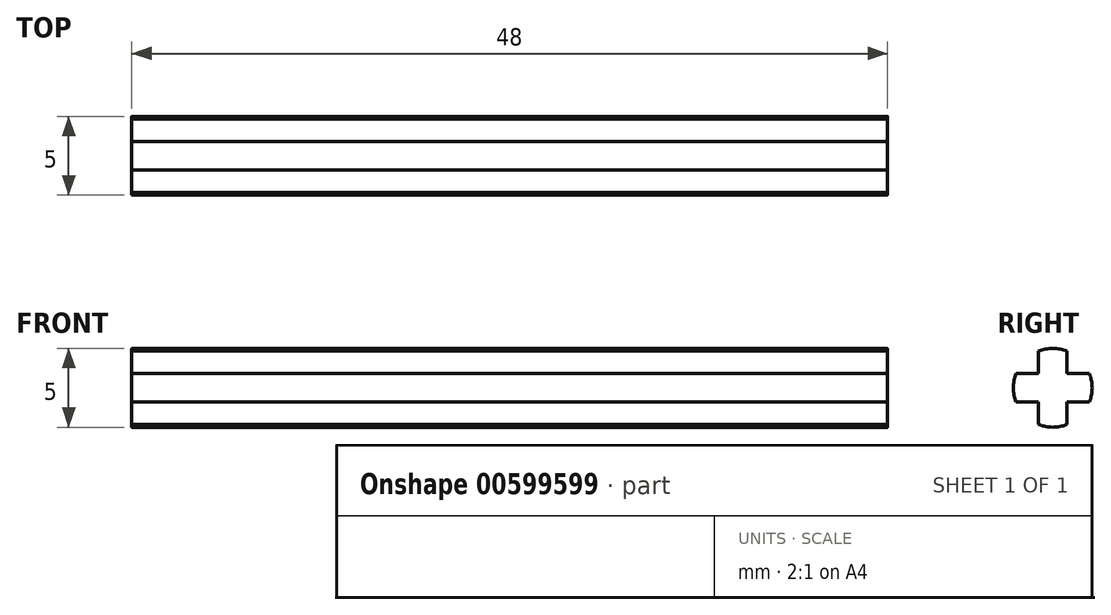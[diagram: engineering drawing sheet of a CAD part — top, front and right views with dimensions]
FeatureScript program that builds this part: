
annotation { "Feature Type Name" : "Feature", "Feature Type Description" : "" }
export const myFeature = defineFeature(function(context is Context, id is Id, definition is map)
    precondition{}
    {
        {
            var Q0;
            Q0=qCreatedBy(makeId("Right.planeOp"),FACE);
            var sketch = newSketch(context, id + "F0", { "sketchPlane" : qUnion([Q0])});
            skArc(sketch, "E0", {"start": v(2.33, -0.9) * mm, "mid": v(2.5, 0) * mm, "end": v(2.33, 0.9) * mm});
            skLineSegment(sketch, "E1.left", {"start": v(-0.9, 2.33) * mm, "end": v(-0.9, 0.9) * mm});
            skLineSegment(sketch, "E1.right", {"start": v(0.9, 2.33) * mm, "end": v(0.9, 0.9) * mm});
            skLineSegment(sketch, "E2.bottom", {"start": v(2.33, 0.9) * mm, "end": v(0.9, 0.9) * mm});
            skLineSegment(sketch, "E2.top", {"start": v(2.33, -0.9) * mm, "end": v(0.9, -0.9) * mm});
            skArc(sketch, "E3.trimOffspring", {"start": v(0.9, 2.33) * mm, "mid": v(0, 2.5) * mm, "end": v(-0.9, 2.33) * mm});
            skArc(sketch, "E4.trimOffspring", {"start": v(-2.33, 0.9) * mm, "mid": v(-2.5, 0) * mm, "end": v(-2.33, -0.9) * mm});
            skArc(sketch, "E5.trimOffspring", {"start": v(-0.9, -2.33) * mm, "mid": v(0, -2.5) * mm, "end": v(0.9, -2.33) * mm});
            skLineSegment(sketch, "E6.trimOffspring", {"start": v(-0.9, -0.9) * mm, "end": v(-0.9, -2.33) * mm});
            skLineSegment(sketch, "E7.trimOffspring", {"start": v(-0.9, 0.9) * mm, "end": v(-2.33, 0.9) * mm});
            skLineSegment(sketch, "E8.trimOffspring", {"start": v(0.9, -0.9) * mm, "end": v(0.9, -2.33) * mm});
            skLineSegment(sketch, "E9.trimOffspring", {"start": v(-0.9, -0.9) * mm, "end": v(-2.33, -0.9) * mm});
            skSolve(sketch);
        }
        {
            var Q0;
            Q0 = qSketchRegion(id + "F0", true);
            extrude(context, id + "F1", {"entities" : qUnion([Q0]), "depth" : 48 * mm, "offsetDistance" : 25 * mm});
        }
    });
